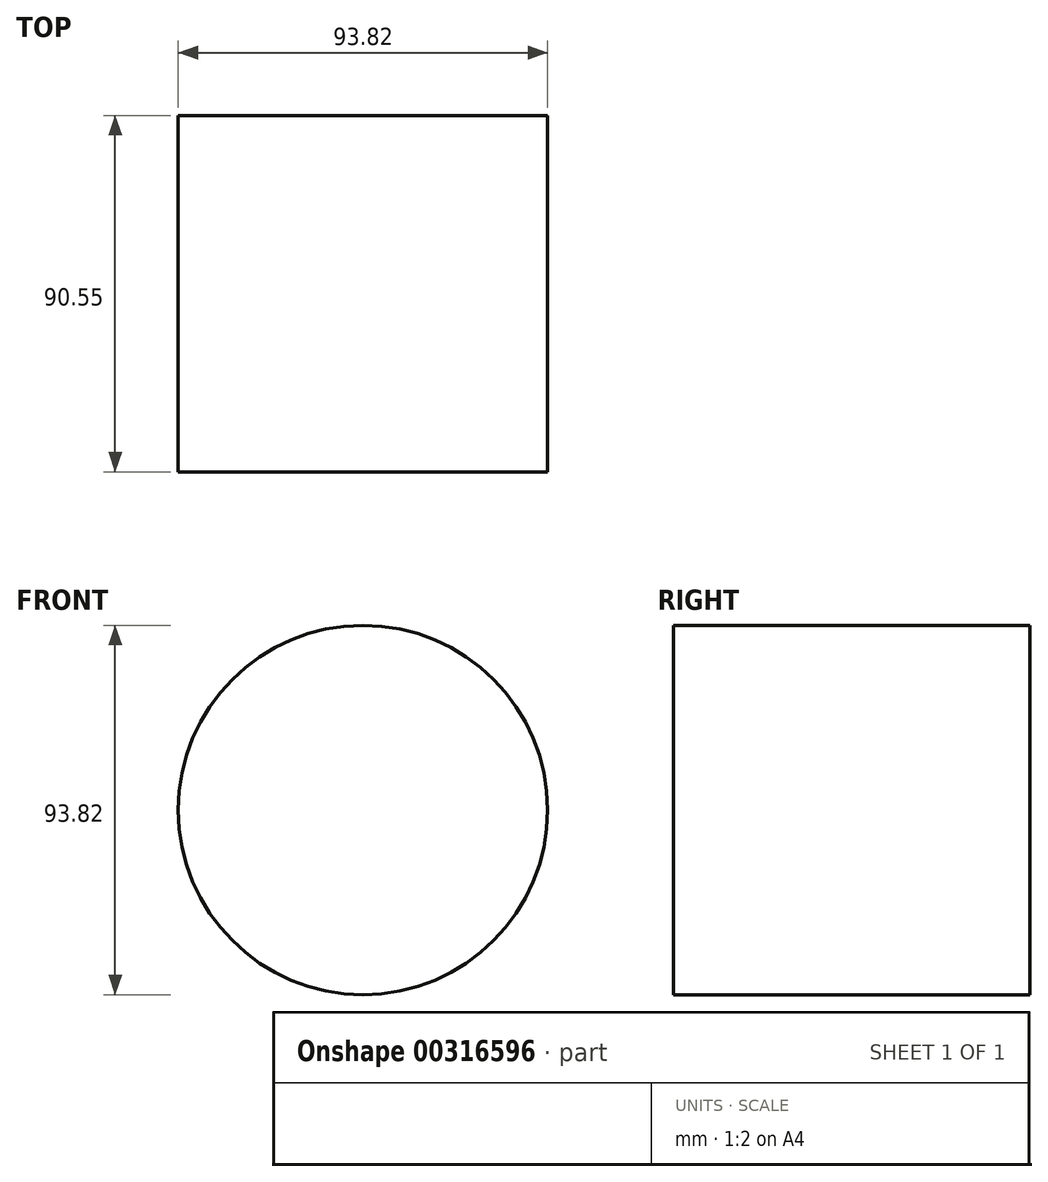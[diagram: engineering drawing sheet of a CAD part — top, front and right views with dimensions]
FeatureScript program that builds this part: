
annotation { "Feature Type Name" : "Feature", "Feature Type Description" : "" }
export const myFeature = defineFeature(function(context is Context, id is Id, definition is map)
    precondition{}
    {
        {
            var Q0;
            Q0=qCreatedBy(makeId("Front.planeOp"),FACE);
            var sketch = newSketch(context, id + "F0", { "sketchPlane" : qUnion([Q0])});
            skCircle(sketch, "E0", {"center": v(0, 0) * mm, "radius": 46.9 * mm});
            skSolve(sketch);
        }
        {
            var Q0;
            Q0=makeQuery(id+"F0.imprint","IMPRINT",FACE,{"disambiguationData":[TD([[makeQuery(id+"F0.imprint","IMPRINT",EDGE,{"derivedFrom":sQuery(id+"F0.wireOp",EDGE,"E0")}),1.0]])]});
            extrude(context, id + "F1", {"entities" : qUnion([Q0]), "depth" : 90.55 * mm});
        }
    });
